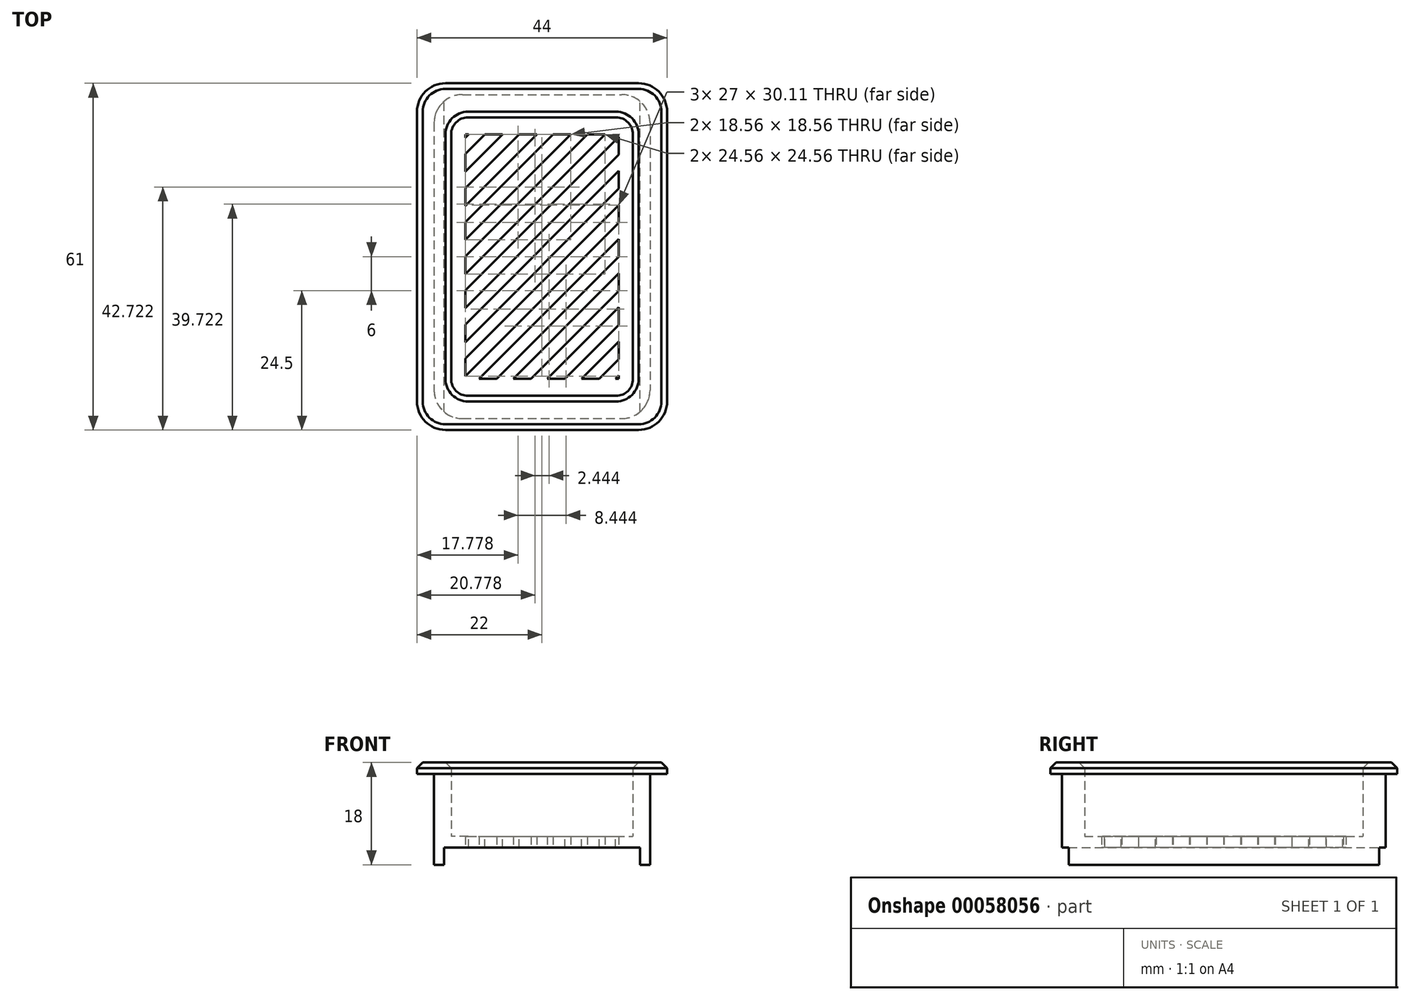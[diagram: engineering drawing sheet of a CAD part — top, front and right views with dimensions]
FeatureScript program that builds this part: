
annotation { "Feature Type Name" : "Feature", "Feature Type Description" : "" }
export const myFeature = defineFeature(function(context is Context, id is Id, definition is map)
    precondition{}
    {
        {
            var Q0;
            Q0=qCreatedBy(makeId("Top.planeOp"),FACE);
            var sketch = newSketch(context, id + "F0", { "sketchPlane" : qUnion([Q0])});
            skLineSegment(sketch, "E0.bottom", {"start": v(0, 0) * mm, "end": v(-28, 0) * mm});
            skLineSegment(sketch, "E0.top", {"start": v(0, 44) * mm, "end": v(-28, 44) * mm});
            skLineSegment(sketch, "E0.left", {"start": v(0, 0) * mm, "end": v(0, 44) * mm});
            skLineSegment(sketch, "E0.right", {"start": v(-28, 0) * mm, "end": v(-28, 44) * mm});
            skSolve(sketch);
        }
        {
            var Q0;
            Q0 = qSketchRegion(id + "F0", true);
            extrude(context, id + "F1", {"entities" : qUnion([Q0]), "depth" : 2 * mm});
        }
        {
            var Q0;
            Q0=makeQuery(id+"F1.opExtrude","CAP_FACE",FACE,{"disambiguationData":[OSD([sQuery(id+"F0.wireOp",EDGE,"E0.bottom"),sQuery(id+"F0.wireOp",EDGE,"E0.top"),sQuery(id+"F0.wireOp",EDGE,"E0.left"),sQuery(id+"F0.wireOp",EDGE,"E0.right")])],"isStart":false});
            var sketch = newSketch(context, id + "F2", { "sketchPlane" : qUnion([Q0])});
            skLineSegment(sketch, "E1.bottom", {"start": v(-29.56, -34) * mm, "end": v(0, -4.44) * mm});
            skLineSegment(sketch, "E1.top", {"start": v(-28, -35.56) * mm, "end": v(1.56, -6) * mm});
            skLineSegment(sketch, "E1.left", {"start": v(-29.56, -34) * mm, "end": v(-28, -35.56) * mm});
            skLineSegment(sketch, "E1.right", {"start": v(0, -4.44) * mm, "end": v(1.56, -6) * mm});
            skLineSegment(sketch, "E2.0.1.0", {"start": v(-28, -29.56) * mm, "end": v(1.56, 0) * mm});
            skLineSegment(sketch, "E2.0.1.1", {"start": v(-29.56, -28) * mm, "end": v(0, 1.56) * mm});
            skLineSegment(sketch, "E2.0.1.2", {"start": v(0, 1.56) * mm, "end": v(1.56, 0) * mm});
            skLineSegment(sketch, "E2.0.1.3", {"start": v(-29.56, -28) * mm, "end": v(-28, -29.56) * mm});
            skLineSegment(sketch, "E2.0.2.0", {"start": v(-28, -23.56) * mm, "end": v(1.56, 6) * mm});
            skLineSegment(sketch, "E2.0.2.1", {"start": v(-29.56, -22) * mm, "end": v(0, 7.56) * mm});
            skLineSegment(sketch, "E2.0.2.2", {"start": v(0, 7.56) * mm, "end": v(1.56, 6) * mm});
            skLineSegment(sketch, "E2.0.2.3", {"start": v(-29.56, -22) * mm, "end": v(-28, -23.56) * mm});
            skLineSegment(sketch, "E2.0.3.0", {"start": v(-28, -17.56) * mm, "end": v(1.56, 12) * mm});
            skLineSegment(sketch, "E2.0.3.1", {"start": v(-29.56, -16) * mm, "end": v(0, 13.56) * mm});
            skLineSegment(sketch, "E2.0.3.2", {"start": v(0, 13.56) * mm, "end": v(1.56, 12) * mm});
            skLineSegment(sketch, "E2.0.3.3", {"start": v(-29.56, -16) * mm, "end": v(-28, -17.56) * mm});
            skLineSegment(sketch, "E2.0.4.0", {"start": v(-28, -11.56) * mm, "end": v(1.56, 18) * mm});
            skLineSegment(sketch, "E2.0.4.1", {"start": v(-29.56, -10) * mm, "end": v(0, 19.56) * mm});
            skLineSegment(sketch, "E2.0.4.2", {"start": v(0, 19.56) * mm, "end": v(1.56, 18) * mm});
            skLineSegment(sketch, "E2.0.4.3", {"start": v(-29.56, -10) * mm, "end": v(-28, -11.56) * mm});
            skLineSegment(sketch, "E2.0.5.0", {"start": v(-28, -5.56) * mm, "end": v(1.56, 24) * mm});
            skLineSegment(sketch, "E2.0.5.1", {"start": v(-29.56, -4) * mm, "end": v(0, 25.56) * mm});
            skLineSegment(sketch, "E2.0.5.2", {"start": v(0, 25.56) * mm, "end": v(1.56, 24) * mm});
            skLineSegment(sketch, "E2.0.5.3", {"start": v(-29.56, -4) * mm, "end": v(-28, -5.56) * mm});
            skLineSegment(sketch, "E2.0.6.0", {"start": v(-28, 0.44) * mm, "end": v(1.56, 30) * mm});
            skLineSegment(sketch, "E2.0.6.1", {"start": v(-29.56, 2) * mm, "end": v(0, 31.56) * mm});
            skLineSegment(sketch, "E2.0.6.2", {"start": v(0, 31.56) * mm, "end": v(1.56, 30) * mm});
            skLineSegment(sketch, "E2.0.6.3", {"start": v(-29.56, 2) * mm, "end": v(-28, 0.44) * mm});
            skLineSegment(sketch, "E2.0.7.0", {"start": v(-28, 6.44) * mm, "end": v(1.56, 36) * mm});
            skLineSegment(sketch, "E2.0.7.1", {"start": v(-29.56, 8) * mm, "end": v(0, 37.56) * mm});
            skLineSegment(sketch, "E2.0.7.2", {"start": v(0, 37.56) * mm, "end": v(1.56, 36) * mm});
            skLineSegment(sketch, "E2.0.7.3", {"start": v(-29.56, 8) * mm, "end": v(-28, 6.44) * mm});
            skLineSegment(sketch, "E2.0.8.0", {"start": v(-28, 12.44) * mm, "end": v(1.56, 42) * mm});
            skLineSegment(sketch, "E2.0.8.1", {"start": v(-29.56, 14) * mm, "end": v(0, 43.56) * mm});
            skLineSegment(sketch, "E2.0.8.2", {"start": v(0, 43.56) * mm, "end": v(1.56, 42) * mm});
            skLineSegment(sketch, "E2.0.8.3", {"start": v(-29.56, 14) * mm, "end": v(-28, 12.44) * mm});
            skLineSegment(sketch, "E2.0.9.0", {"start": v(-28, 18.44) * mm, "end": v(1.56, 48) * mm});
            skLineSegment(sketch, "E2.0.9.1", {"start": v(-29.56, 20) * mm, "end": v(0, 49.56) * mm});
            skLineSegment(sketch, "E2.0.9.2", {"start": v(0, 49.56) * mm, "end": v(1.56, 48) * mm});
            skLineSegment(sketch, "E2.0.9.3", {"start": v(-29.56, 20) * mm, "end": v(-28, 18.44) * mm});
            skLineSegment(sketch, "E2.0.10.0", {"start": v(-28, 24.44) * mm, "end": v(1.56, 54) * mm});
            skLineSegment(sketch, "E2.0.10.1", {"start": v(-29.56, 26) * mm, "end": v(0, 55.56) * mm});
            skLineSegment(sketch, "E2.0.10.2", {"start": v(0, 55.56) * mm, "end": v(1.56, 54) * mm});
            skLineSegment(sketch, "E2.0.10.3", {"start": v(-29.56, 26) * mm, "end": v(-28, 24.44) * mm});
            skLineSegment(sketch, "E2.0.11.0", {"start": v(-28, 30.44) * mm, "end": v(1.56, 60) * mm});
            skLineSegment(sketch, "E2.0.11.1", {"start": v(-29.56, 32) * mm, "end": v(0, 61.56) * mm});
            skLineSegment(sketch, "E2.0.11.2", {"start": v(0, 61.56) * mm, "end": v(1.56, 60) * mm});
            skLineSegment(sketch, "E2.0.11.3", {"start": v(-29.56, 32) * mm, "end": v(-28, 30.44) * mm});
            skLineSegment(sketch, "E2.0.12.0", {"start": v(-28, 36.44) * mm, "end": v(1.56, 66) * mm});
            skLineSegment(sketch, "E2.0.12.1", {"start": v(-29.56, 38) * mm, "end": v(0, 67.56) * mm});
            skLineSegment(sketch, "E2.0.12.2", {"start": v(0, 67.56) * mm, "end": v(1.56, 66) * mm});
            skLineSegment(sketch, "E2.0.12.3", {"start": v(-29.56, 38) * mm, "end": v(-28, 36.44) * mm});
            skLineSegment(sketch, "E2.0.13.0", {"start": v(-28, 42.44) * mm, "end": v(1.56, 72) * mm});
            skLineSegment(sketch, "E2.0.13.1", {"start": v(-29.56, 44) * mm, "end": v(0, 73.56) * mm});
            skLineSegment(sketch, "E2.0.13.2", {"start": v(0, 73.56) * mm, "end": v(1.56, 72) * mm});
            skLineSegment(sketch, "E2.0.13.3", {"start": v(-29.56, 44) * mm, "end": v(-28, 42.44) * mm});
            skLineSegment(sketch, "E2.0.14.0", {"start": v(-28, 48.44) * mm, "end": v(1.56, 78) * mm});
            skLineSegment(sketch, "E2.0.14.1", {"start": v(-29.56, 50) * mm, "end": v(0, 79.56) * mm});
            skLineSegment(sketch, "E2.0.14.2", {"start": v(0, 79.56) * mm, "end": v(1.56, 78) * mm});
            skLineSegment(sketch, "E2.0.14.3", {"start": v(-29.56, 50) * mm, "end": v(-28, 48.44) * mm});
            skLineSegment(sketch, "E2.direction1", {"start": v(-28, -35.56) * mm, "end": v(-5, -35.56) * mm, "construction": true});
            skLineSegment(sketch, "E2.direction2", {"start": v(-28, -35.56) * mm, "end": v(-28, -29.56) * mm, "construction": true});
            skLineSegment(sketch, "E3", {"start": v(0, 79.56) * mm, "end": v(-28, -35.56) * mm});
            skPoint(sketch, "E4", {"position": v(-14, 22) * mm});
            skPoint(sketch, "E5", {"position": v(0, 22) * mm});
            skPoint(sketch, "E6", {"position": v(-13.22, 44) * mm});
            skPoint(sketch, "E6.positionSnap0", {"position": v(-13.22, -14.78) * mm});
            skSolve(sketch);
        }
        {
            var Q0;
            Q0 = qSketchRegion(id + "F2", true);
            var Q1;
            Q1=makeQuery(id+"F1.opExtrude","CAP_FACE",FACE,{"disambiguationData":[OSD([sQuery(id+"F0.wireOp",EDGE,"E0.bottom"),sQuery(id+"F0.wireOp",EDGE,"E0.top"),sQuery(id+"F0.wireOp",EDGE,"E0.left"),sQuery(id+"F0.wireOp",EDGE,"E0.right")])],"isStart":true});
            extrude(context, id + "F3", {"entities" : qUnion([Q0]), "operationType" : NewBodyOperationType.REMOVE, "endBound" : BoundingType.UP_TO_SURFACE, "oppositeDirection" : true, "endBoundEntityFace" : qUnion([Q1]), "depth" : 25 * mm});
        }
        {
            var Q0;
            Q0=qCreatedBy(makeId("Top.planeOp"),FACE);
            var sketch = newSketch(context, id + "F4", { "sketchPlane" : qUnion([Q0])});
            skLineSegment(sketch, "E7.bottom", {"start": v(-33, 50.5) * mm, "end": v(5, 50.5) * mm});
            skLineSegment(sketch, "E7.top", {"start": v(-33, -6.5) * mm, "end": v(5, -6.5) * mm});
            skLineSegment(sketch, "E7.left", {"start": v(-33, 50.5) * mm, "end": v(-33, -6.5) * mm});
            skLineSegment(sketch, "E7.right", {"start": v(5, 50.5) * mm, "end": v(5, -6.5) * mm});
            skLineSegment(sketch, "E8.bottom", {"start": v(-27.5, 43.5) * mm, "end": v(-0.5, 43.5) * mm});
            skLineSegment(sketch, "E8.top", {"start": v(-27.5, 0.5) * mm, "end": v(-0.5, 0.5) * mm});
            skLineSegment(sketch, "E8.left", {"start": v(-27.5, 43.5) * mm, "end": v(-27.5, 0.5) * mm});
            skLineSegment(sketch, "E8.right", {"start": v(-0.5, 43.5) * mm, "end": v(-0.5, 0.5) * mm});
            skPoint(sketch, "E9", {"position": v(-14, 50.5) * mm});
            skPoint(sketch, "E10", {"position": v(5, 22) * mm});
            skPoint(sketch, "E11", {"position": v(-0.5, 22) * mm});
            skPoint(sketch, "E12", {"position": v(-14, 43.5) * mm});
            skPoint(sketch, "E13", {"position": v(-14, 0) * mm});
            skPoint(sketch, "E14", {"position": v(-28, 22) * mm});
            skSolve(sketch);
        }
        {
            var Q0;
            Q0 = qSketchRegion(id + "F4", true);
            extrude(context, id + "F5", {"entities" : qUnion([Q0]), "operationType" : NewBodyOperationType.ADD, "depth" : 2 * mm});
        }
        {
            var Q0;
            {var subQ0=sQuery(id+"F0.wireOp",EDGE,"E0.top");var subQ2=sQuery(id+"F0.wireOp",EDGE,"E0.right");var subQ4=sQuery(id+"F0.wireOp",EDGE,"E0.left");var subQ5=sQuery(id+"F0.wireOp",EDGE,"E0.bottom");var subQ6=makeQuery(id+"F1.opExtrude","CAP_FACE",FACE,{"disambiguationData":[OSD([subQ5,subQ0,subQ4,subQ2])],"isStart":true});Q0=makeQuery(id+"F5.boolean.opBoolean","MERGE",FACE,{"derivedFrom":[makeQuery(id+"F3.boolean.opBoolean","SPLIT",FACE,{"disambiguationData":[TD([makeQuery(id+"F3.opExtrude","SWEPT_FACE",FACE,{"disambiguationData":[OSD([sQuery(id+"F2.wireOp",EDGE,"E1.bottom")])]})])],"derivedFrom":subQ6}),makeQuery(id+"F3.boolean.opBoolean","SPLIT",FACE,{"disambiguationData":[TD([makeQuery(id+"F3.opExtrude","SWEPT_FACE",FACE,{"disambiguationData":[OSD([sQuery(id+"F2.wireOp",EDGE,"E2.0.1.1")])]})])],"derivedFrom":subQ6}),makeQuery(id+"F3.boolean.opBoolean","SPLIT",FACE,{"disambiguationData":[TD([makeQuery(id+"F3.opExtrude","SWEPT_FACE",FACE,{"disambiguationData":[OSD([sQuery(id+"F2.wireOp",EDGE,"E2.0.2.1")])]})])],"derivedFrom":subQ6}),makeQuery(id+"F3.boolean.opBoolean","SPLIT",FACE,{"disambiguationData":[TD([makeQuery(id+"F3.opExtrude","SWEPT_FACE",FACE,{"disambiguationData":[OSD([sQuery(id+"F2.wireOp",EDGE,"E2.0.3.1")])]})])],"derivedFrom":subQ6}),makeQuery(id+"F3.boolean.opBoolean","SPLIT",FACE,{"disambiguationData":[TD([makeQuery(id+"F3.opExtrude","SWEPT_FACE",FACE,{"disambiguationData":[OSD([sQuery(id+"F2.wireOp",EDGE,"E2.0.4.1")])]})])],"derivedFrom":subQ6}),makeQuery(id+"F3.boolean.opBoolean","SPLIT",FACE,{"disambiguationData":[TD([makeQuery(id+"F3.opExtrude","SWEPT_FACE",FACE,{"disambiguationData":[OSD([sQuery(id+"F2.wireOp",EDGE,"E2.0.5.1")])]})])],"derivedFrom":subQ6}),makeQuery(id+"F3.boolean.opBoolean","SPLIT",FACE,{"disambiguationData":[TD([makeQuery(id+"F3.opExtrude","SWEPT_FACE",FACE,{"disambiguationData":[OSD([sQuery(id+"F2.wireOp",EDGE,"E2.0.6.1")])]})])],"derivedFrom":subQ6}),makeQuery(id+"F3.boolean.opBoolean","SPLIT",FACE,{"disambiguationData":[TD([makeQuery(id+"F3.opExtrude","SWEPT_FACE",FACE,{"disambiguationData":[OSD([sQuery(id+"F2.wireOp",EDGE,"E2.0.7.1")])]})])],"derivedFrom":subQ6}),makeQuery(id+"F3.boolean.opBoolean","SPLIT",FACE,{"disambiguationData":[TD([makeQuery(id+"F3.opExtrude","SWEPT_FACE",FACE,{"disambiguationData":[OSD([sQuery(id+"F2.wireOp",EDGE,"E2.0.8.1")])]})])],"derivedFrom":subQ6}),makeQuery(id+"F3.boolean.opBoolean","SPLIT",FACE,{"disambiguationData":[TD([makeQuery(id+"F3.opExtrude","SWEPT_FACE",FACE,{"disambiguationData":[OSD([sQuery(id+"F2.wireOp",EDGE,"E2.0.9.1")])]})])],"derivedFrom":subQ6}),makeQuery(id+"F3.boolean.opBoolean","SPLIT",FACE,{"disambiguationData":[TD([makeQuery(id+"F3.opExtrude","SWEPT_FACE",FACE,{"disambiguationData":[OSD([sQuery(id+"F2.wireOp",EDGE,"E2.0.10.1")])]})])],"derivedFrom":subQ6}),makeQuery(id+"F3.boolean.opBoolean","SPLIT",FACE,{"disambiguationData":[TD([makeQuery(id+"F3.opExtrude","SWEPT_FACE",FACE,{"disambiguationData":[OSD([sQuery(id+"F2.wireOp",EDGE,"E2.0.11.1")])]})])],"derivedFrom":subQ6}),makeQuery(id+"F3.boolean.opBoolean","SPLIT",FACE,{"disambiguationData":[TD([makeQuery(id+"F3.opExtrude","SWEPT_FACE",FACE,{"disambiguationData":[OSD([sQuery(id+"F2.wireOp",EDGE,"E2.0.12.1")])]})])],"derivedFrom":subQ6}),makeQuery(id+"F3.boolean.opBoolean","SPLIT",FACE,{"disambiguationData":[TD([makeQuery(id+"F3.opExtrude","SWEPT_FACE",FACE,{"disambiguationData":[OSD([sQuery(id+"F2.wireOp",EDGE,"E2.0.13.1")])]})])],"derivedFrom":subQ6}),makeQuery(id+"F5.opExtrude","CAP_FACE",FACE,{"disambiguationData":[OSD([sQuery(id+"F4.wireOp",EDGE,"E7.bottom"),sQuery(id+"F4.wireOp",EDGE,"E7.top"),sQuery(id+"F4.wireOp",EDGE,"E7.left"),sQuery(id+"F4.wireOp",EDGE,"E7.right"),sQuery(id+"F4.wireOp",EDGE,"E8.bottom"),sQuery(id+"F4.wireOp",EDGE,"E8.top"),sQuery(id+"F4.wireOp",EDGE,"E8.left"),sQuery(id+"F4.wireOp",EDGE,"E8.right")])],"isStart":true})]});}
            var sketch = newSketch(context, id + "F6", { "sketchPlane" : qUnion([Q0])});
            skLineSegment(sketch, "E15.bottom", {"start": v(-33, 6.5) * mm, "end": v(-31.25, 6.5) * mm});
            skLineSegment(sketch, "E15.top", {"start": v(-33, -50.5) * mm, "end": v(-31.25, -50.5) * mm});
            skLineSegment(sketch, "E15.left", {"start": v(-33, 6.5) * mm, "end": v(-33, -50.5) * mm});
            skLineSegment(sketch, "E15.right", {"start": v(-31.25, 6.5) * mm, "end": v(-31.25, -50.5) * mm});
            skLineSegment(sketch, "E16.bottom", {"start": v(5, 6.5) * mm, "end": v(3.25, 6.5) * mm});
            skLineSegment(sketch, "E16.top", {"start": v(5, -50.5) * mm, "end": v(3.25, -50.5) * mm});
            skLineSegment(sketch, "E16.left", {"start": v(5, 6.5) * mm, "end": v(5, -50.5) * mm});
            skLineSegment(sketch, "E16.right", {"start": v(3.25, 6.5) * mm, "end": v(3.25, -50.5) * mm});
            skSolve(sketch);
        }
        {
            var Q0;
            Q0 = qSketchRegion(id + "F6", true);
            extrude(context, id + "F7", {"entities" : qUnion([Q0]), "operationType" : NewBodyOperationType.ADD, "depth" : 3 * mm});
        }
        {
            var Q0;
            {var subQ0=sQuery(id+"F0.wireOp",EDGE,"E0.top");var subQ2=sQuery(id+"F0.wireOp",EDGE,"E0.right");var subQ4=sQuery(id+"F0.wireOp",EDGE,"E0.left");var subQ5=sQuery(id+"F0.wireOp",EDGE,"E0.bottom");var subQ6=makeQuery(id+"F1.opExtrude","CAP_FACE",FACE,{"disambiguationData":[OSD([subQ5,subQ0,subQ4,subQ2])],"isStart":false});Q0=makeQuery(id+"F5.boolean.opBoolean","MERGE",FACE,{"derivedFrom":[makeQuery(id+"F3.boolean.opBoolean","SPLIT",FACE,{"disambiguationData":[TD([makeQuery(id+"F3.opExtrude","SWEPT_FACE",FACE,{"disambiguationData":[OSD([sQuery(id+"F2.wireOp",EDGE,"E1.bottom")])]})])],"derivedFrom":subQ6}),makeQuery(id+"F3.boolean.opBoolean","SPLIT",FACE,{"disambiguationData":[TD([makeQuery(id+"F3.opExtrude","SWEPT_FACE",FACE,{"disambiguationData":[OSD([sQuery(id+"F2.wireOp",EDGE,"E2.0.1.1")])]})])],"derivedFrom":subQ6}),makeQuery(id+"F3.boolean.opBoolean","SPLIT",FACE,{"disambiguationData":[TD([makeQuery(id+"F3.opExtrude","SWEPT_FACE",FACE,{"disambiguationData":[OSD([sQuery(id+"F2.wireOp",EDGE,"E2.0.2.1")])]})])],"derivedFrom":subQ6}),makeQuery(id+"F3.boolean.opBoolean","SPLIT",FACE,{"disambiguationData":[TD([makeQuery(id+"F3.opExtrude","SWEPT_FACE",FACE,{"disambiguationData":[OSD([sQuery(id+"F2.wireOp",EDGE,"E2.0.3.1")])]})])],"derivedFrom":subQ6}),makeQuery(id+"F3.boolean.opBoolean","SPLIT",FACE,{"disambiguationData":[TD([makeQuery(id+"F3.opExtrude","SWEPT_FACE",FACE,{"disambiguationData":[OSD([sQuery(id+"F2.wireOp",EDGE,"E2.0.4.1")])]})])],"derivedFrom":subQ6}),makeQuery(id+"F3.boolean.opBoolean","SPLIT",FACE,{"disambiguationData":[TD([makeQuery(id+"F3.opExtrude","SWEPT_FACE",FACE,{"disambiguationData":[OSD([sQuery(id+"F2.wireOp",EDGE,"E2.0.5.1")])]})])],"derivedFrom":subQ6}),makeQuery(id+"F3.boolean.opBoolean","SPLIT",FACE,{"disambiguationData":[TD([makeQuery(id+"F3.opExtrude","SWEPT_FACE",FACE,{"disambiguationData":[OSD([sQuery(id+"F2.wireOp",EDGE,"E2.0.6.1")])]})])],"derivedFrom":subQ6}),makeQuery(id+"F3.boolean.opBoolean","SPLIT",FACE,{"disambiguationData":[TD([makeQuery(id+"F3.opExtrude","SWEPT_FACE",FACE,{"disambiguationData":[OSD([sQuery(id+"F2.wireOp",EDGE,"E2.0.7.1")])]})])],"derivedFrom":subQ6}),makeQuery(id+"F3.boolean.opBoolean","SPLIT",FACE,{"disambiguationData":[TD([makeQuery(id+"F3.opExtrude","SWEPT_FACE",FACE,{"disambiguationData":[OSD([sQuery(id+"F2.wireOp",EDGE,"E2.0.8.1")])]})])],"derivedFrom":subQ6}),makeQuery(id+"F3.boolean.opBoolean","SPLIT",FACE,{"disambiguationData":[TD([makeQuery(id+"F3.opExtrude","SWEPT_FACE",FACE,{"disambiguationData":[OSD([sQuery(id+"F2.wireOp",EDGE,"E2.0.9.1")])]})])],"derivedFrom":subQ6}),makeQuery(id+"F3.boolean.opBoolean","SPLIT",FACE,{"disambiguationData":[TD([makeQuery(id+"F3.opExtrude","SWEPT_FACE",FACE,{"disambiguationData":[OSD([sQuery(id+"F2.wireOp",EDGE,"E2.0.10.1")])]})])],"derivedFrom":subQ6}),makeQuery(id+"F3.boolean.opBoolean","SPLIT",FACE,{"disambiguationData":[TD([makeQuery(id+"F3.opExtrude","SWEPT_FACE",FACE,{"disambiguationData":[OSD([sQuery(id+"F2.wireOp",EDGE,"E2.0.11.1")])]})])],"derivedFrom":subQ6}),makeQuery(id+"F3.boolean.opBoolean","SPLIT",FACE,{"disambiguationData":[TD([makeQuery(id+"F3.opExtrude","SWEPT_FACE",FACE,{"disambiguationData":[OSD([sQuery(id+"F2.wireOp",EDGE,"E2.0.12.1")])]})])],"derivedFrom":subQ6}),makeQuery(id+"F3.boolean.opBoolean","SPLIT",FACE,{"disambiguationData":[TD([makeQuery(id+"F3.opExtrude","SWEPT_FACE",FACE,{"disambiguationData":[OSD([sQuery(id+"F2.wireOp",EDGE,"E2.0.13.1")])]})])],"derivedFrom":subQ6}),makeQuery(id+"F5.opExtrude","CAP_FACE",FACE,{"disambiguationData":[OSD([sQuery(id+"F4.wireOp",EDGE,"E7.bottom"),sQuery(id+"F4.wireOp",EDGE,"E7.top"),sQuery(id+"F4.wireOp",EDGE,"E7.left"),sQuery(id+"F4.wireOp",EDGE,"E7.right"),sQuery(id+"F4.wireOp",EDGE,"E8.bottom"),sQuery(id+"F4.wireOp",EDGE,"E8.top"),sQuery(id+"F4.wireOp",EDGE,"E8.left"),sQuery(id+"F4.wireOp",EDGE,"E8.right")])],"isStart":false})]});}
            var sketch = newSketch(context, id + "F8", { "sketchPlane" : qUnion([Q0])});
            skLineSegment(sketch, "E17.bottom", {"start": v(-33, 50.5) * mm, "end": v(5, 50.5) * mm});
            skLineSegment(sketch, "E17.top", {"start": v(-33, -6.5) * mm, "end": v(5, -6.5) * mm});
            skLineSegment(sketch, "E17.left", {"start": v(-33, 50.5) * mm, "end": v(-33, -6.5) * mm});
            skLineSegment(sketch, "E17.right", {"start": v(5, 50.5) * mm, "end": v(5, -6.5) * mm});
            skLineSegment(sketch, "E18.bottom", {"start": v(-30, 46.5) * mm, "end": v(2, 46.5) * mm});
            skLineSegment(sketch, "E18.top", {"start": v(-30, -2.5) * mm, "end": v(2, -2.5) * mm});
            skLineSegment(sketch, "E18.left", {"start": v(-30, 46.5) * mm, "end": v(-30, -2.5) * mm});
            skLineSegment(sketch, "E18.right", {"start": v(2, 46.5) * mm, "end": v(2, -2.5) * mm});
            skSolve(sketch);
        }
        {
            var Q0;
            Q0 = qSketchRegion(id + "F8", true);
            extrude(context, id + "F9", {"entities" : qUnion([Q0]), "operationType" : NewBodyOperationType.ADD, "depth" : 11 * mm});
        }
        {
            var Q0;
            Q0=makeQuery(id+"F9.opExtrude","CAP_FACE",FACE,{"disambiguationData":[OSD([sQuery(id+"F8.wireOp",EDGE,"E17.bottom"),sQuery(id+"F8.wireOp",EDGE,"E17.top"),sQuery(id+"F8.wireOp",EDGE,"E17.left"),sQuery(id+"F8.wireOp",EDGE,"E17.right"),sQuery(id+"F8.wireOp",EDGE,"E18.bottom"),sQuery(id+"F8.wireOp",EDGE,"E18.top"),sQuery(id+"F8.wireOp",EDGE,"E18.left"),sQuery(id+"F8.wireOp",EDGE,"E18.right")])],"isStart":false});
            var sketch = newSketch(context, id + "F10", { "sketchPlane" : qUnion([Q0])});
            skLineSegment(sketch, "E19.bottom", {"start": v(-36, 52.5) * mm, "end": v(8, 52.5) * mm});
            skLineSegment(sketch, "E19.top", {"start": v(-36, -8.5) * mm, "end": v(8, -8.5) * mm});
            skLineSegment(sketch, "E19.left", {"start": v(-36, 52.5) * mm, "end": v(-36, -8.5) * mm});
            skLineSegment(sketch, "E19.right", {"start": v(8, 52.5) * mm, "end": v(8, -8.5) * mm});
            skLineSegment(sketch, "E20.bottom", {"start": v(2, -2.5) * mm, "end": v(-30, -2.5) * mm});
            skLineSegment(sketch, "E20.top", {"start": v(2, 46.5) * mm, "end": v(-30, 46.5) * mm});
            skLineSegment(sketch, "E20.left", {"start": v(2, -2.5) * mm, "end": v(2, 46.5) * mm});
            skLineSegment(sketch, "E20.right", {"start": v(-30, -2.5) * mm, "end": v(-30, 46.5) * mm});
            skSolve(sketch);
        }
        {
            var Q0;
            Q0 = qSketchRegion(id + "F10", true);
            extrude(context, id + "F11", {"entities" : qUnion([Q0]), "operationType" : NewBodyOperationType.ADD, "depth" : 2 * mm});
        }
        {
            var Q0;
            Q0=makeQuery(id+"F11.opExtrude","SWEPT_EDGE",EDGE,{"disambiguationData":[OSD([sQuery(id+"F10.wireOp",EDGE,"E19.top"),sQuery(id+"F10.wireOp",EDGE,"E19.right")])]});
            var Q1;
            Q1=makeQuery(id+"F9.boolean.opBoolean","MERGE",EDGE,{"derivedFrom":[makeQuery(id+"F7.boolean.opBoolean","MERGE",EDGE,{"derivedFrom":[makeQuery(id+"F5.opExtrude","SWEPT_EDGE",EDGE,{"disambiguationData":[OSD([sQuery(id+"F4.wireOp",EDGE,"E7.top"),sQuery(id+"F4.wireOp",EDGE,"E7.right")])]}),makeQuery(id+"F7.opExtrude","SWEPT_EDGE",EDGE,{"disambiguationData":[OSD([sQuery(id+"F6.wireOp",EDGE,"E16.bottom"),sQuery(id+"F6.wireOp",EDGE,"E16.left")])]})]}),makeQuery(id+"F9.opExtrude","SWEPT_EDGE",EDGE,{"disambiguationData":[OSD([sQuery(id+"F8.wireOp",EDGE,"E17.top"),sQuery(id+"F8.wireOp",EDGE,"E17.right")])]})]});
            var Q2;
            Q2=makeQuery(id+"F9.boolean.opBoolean","MERGE",EDGE,{"derivedFrom":[makeQuery(id+"F7.boolean.opBoolean","MERGE",EDGE,{"derivedFrom":[makeQuery(id+"F5.opExtrude","SWEPT_EDGE",EDGE,{"disambiguationData":[OSD([sQuery(id+"F4.wireOp",EDGE,"E7.top"),sQuery(id+"F4.wireOp",EDGE,"E7.left")])]}),makeQuery(id+"F7.opExtrude","SWEPT_EDGE",EDGE,{"disambiguationData":[OSD([sQuery(id+"F6.wireOp",EDGE,"E15.bottom"),sQuery(id+"F6.wireOp",EDGE,"E15.left")])]})]}),makeQuery(id+"F9.opExtrude","SWEPT_EDGE",EDGE,{"disambiguationData":[OSD([sQuery(id+"F8.wireOp",EDGE,"E17.top"),sQuery(id+"F8.wireOp",EDGE,"E17.left")])]})]});
            var Q3;
            Q3=makeQuery(id+"F11.opExtrude","SWEPT_EDGE",EDGE,{"disambiguationData":[OSD([sQuery(id+"F10.wireOp",EDGE,"E19.top"),sQuery(id+"F10.wireOp",EDGE,"E19.left")])]});
            var Q4;
            Q4=makeQuery(id+"F11.opExtrude","SWEPT_EDGE",EDGE,{"disambiguationData":[OSD([sQuery(id+"F10.wireOp",EDGE,"E19.bottom"),sQuery(id+"F10.wireOp",EDGE,"E19.left")])]});
            var Q5;
            Q5=makeQuery(id+"F9.boolean.opBoolean","MERGE",EDGE,{"derivedFrom":[makeQuery(id+"F7.boolean.opBoolean","MERGE",EDGE,{"derivedFrom":[makeQuery(id+"F5.opExtrude","SWEPT_EDGE",EDGE,{"disambiguationData":[OSD([sQuery(id+"F4.wireOp",EDGE,"E7.bottom"),sQuery(id+"F4.wireOp",EDGE,"E7.left")])]}),makeQuery(id+"F7.opExtrude","SWEPT_EDGE",EDGE,{"disambiguationData":[OSD([sQuery(id+"F6.wireOp",EDGE,"E15.top"),sQuery(id+"F6.wireOp",EDGE,"E15.left")])]})]}),makeQuery(id+"F9.opExtrude","SWEPT_EDGE",EDGE,{"disambiguationData":[OSD([sQuery(id+"F8.wireOp",EDGE,"E17.bottom"),sQuery(id+"F8.wireOp",EDGE,"E17.left")])]})]});
            var Q6;
            Q6=makeQuery(id+"F11.opExtrude","SWEPT_EDGE",EDGE,{"disambiguationData":[OSD([sQuery(id+"F10.wireOp",EDGE,"E19.bottom"),sQuery(id+"F10.wireOp",EDGE,"E19.right")])]});
            var Q7;
            Q7=makeQuery(id+"F9.boolean.opBoolean","MERGE",EDGE,{"derivedFrom":[makeQuery(id+"F7.boolean.opBoolean","MERGE",EDGE,{"derivedFrom":[makeQuery(id+"F5.opExtrude","SWEPT_EDGE",EDGE,{"disambiguationData":[OSD([sQuery(id+"F4.wireOp",EDGE,"E7.bottom"),sQuery(id+"F4.wireOp",EDGE,"E7.right")])]}),makeQuery(id+"F7.opExtrude","SWEPT_EDGE",EDGE,{"disambiguationData":[OSD([sQuery(id+"F6.wireOp",EDGE,"E16.top"),sQuery(id+"F6.wireOp",EDGE,"E16.left")])]})]}),makeQuery(id+"F9.opExtrude","SWEPT_EDGE",EDGE,{"disambiguationData":[OSD([sQuery(id+"F8.wireOp",EDGE,"E17.bottom"),sQuery(id+"F8.wireOp",EDGE,"E17.right")])]})]});
            fillet(context, id + "F12", {"entities" : qUnion([Q0, Q1, Q2, Q3, Q4, Q5, Q6, Q7]), "radius" : 5 * mm, "tangentPropagation" : true, "allowEdgeOverflow" : false});
        }
        {
            var Q0;
            Q0=makeQuery(id+"F11.boolean.opBoolean","MERGE",EDGE,{"derivedFrom":[makeQuery(id+"F9.opExtrude","SWEPT_EDGE",EDGE,{"disambiguationData":[OSD([sQuery(id+"F8.wireOp",EDGE,"E18.bottom"),sQuery(id+"F8.wireOp",EDGE,"E18.left")])]}),makeQuery(id+"F11.opExtrude","SWEPT_EDGE",EDGE,{"disambiguationData":[OSD([sQuery(id+"F10.wireOp",EDGE,"E20.top"),sQuery(id+"F10.wireOp",EDGE,"E20.right")])]})]});
            var Q1;
            Q1=makeQuery(id+"F11.boolean.opBoolean","MERGE",EDGE,{"derivedFrom":[makeQuery(id+"F9.opExtrude","SWEPT_EDGE",EDGE,{"disambiguationData":[OSD([sQuery(id+"F8.wireOp",EDGE,"E18.top"),sQuery(id+"F8.wireOp",EDGE,"E18.left")])]}),makeQuery(id+"F11.opExtrude","SWEPT_EDGE",EDGE,{"disambiguationData":[OSD([sQuery(id+"F10.wireOp",EDGE,"E20.bottom"),sQuery(id+"F10.wireOp",EDGE,"E20.right")])]})]});
            var Q2;
            Q2=makeQuery(id+"F11.boolean.opBoolean","MERGE",EDGE,{"derivedFrom":[makeQuery(id+"F9.opExtrude","SWEPT_EDGE",EDGE,{"disambiguationData":[OSD([sQuery(id+"F8.wireOp",EDGE,"E18.bottom"),sQuery(id+"F8.wireOp",EDGE,"E18.right")])]}),makeQuery(id+"F11.opExtrude","SWEPT_EDGE",EDGE,{"disambiguationData":[OSD([sQuery(id+"F10.wireOp",EDGE,"E20.top"),sQuery(id+"F10.wireOp",EDGE,"E20.left")])]})]});
            var Q3;
            Q3=makeQuery(id+"F11.boolean.opBoolean","MERGE",EDGE,{"derivedFrom":[makeQuery(id+"F9.opExtrude","SWEPT_EDGE",EDGE,{"disambiguationData":[OSD([sQuery(id+"F8.wireOp",EDGE,"E18.top"),sQuery(id+"F8.wireOp",EDGE,"E18.right")])]}),makeQuery(id+"F11.opExtrude","SWEPT_EDGE",EDGE,{"disambiguationData":[OSD([sQuery(id+"F10.wireOp",EDGE,"E20.bottom"),sQuery(id+"F10.wireOp",EDGE,"E20.left")])]})]});
            fillet(context, id + "F13", {"entities" : qUnion([Q0, Q1, Q2, Q3]), "radius" : 3 * mm, "tangentPropagation" : true, "allowEdgeOverflow" : false});
        }
        {
            var Q0;
            Q0=makeQuery(id+"F9.opExtrude","CAP_EDGE",EDGE,{"disambiguationData":[OSD([sQuery(id+"F8.wireOp",EDGE,"E18.bottom")])],"isStart":true});
            var Q1;
            Q1=makeQuery(id+"F11.opExtrude","CAP_EDGE",EDGE,{"disambiguationData":[OSD([sQuery(id+"F10.wireOp",EDGE,"E20.top")])],"isStart":false});
            var Q2;
            Q2=makeQuery(id+"F11.opExtrude","CAP_EDGE",EDGE,{"disambiguationData":[OSD([sQuery(id+"F10.wireOp",EDGE,"E19.left")])],"isStart":false});
            chamfer(context, id + "F14", {"entities" : qUnion([Q0, Q1, Q2]), "width" : 1 * mm, "tangentPropagation" : true});
        }
    });
